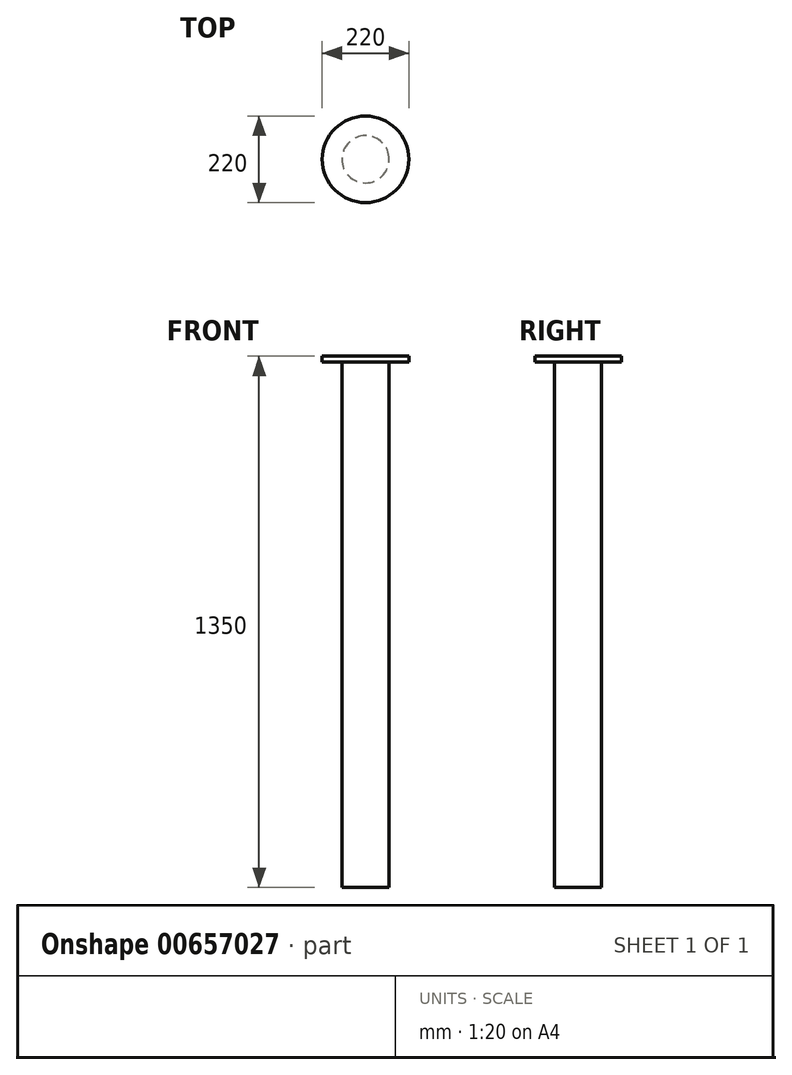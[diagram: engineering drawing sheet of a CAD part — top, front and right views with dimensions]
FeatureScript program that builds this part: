
annotation { "Feature Type Name" : "Feature", "Feature Type Description" : "" }
export const myFeature = defineFeature(function(context is Context, id is Id, definition is map)
    precondition{}
    {
        {
            var Q0;
            Q0=qCreatedBy(makeId("Top.planeOp"),FACE);
            var sketch = newSketch(context, id + "F0", { "sketchPlane" : qUnion([Q0])});
            skCircle(sketch, "E0", {"center": v(0, 0) * mm, "radius": 110 * mm});
            skCircle(sketch, "E1", {"center": v(0, 0) * mm, "radius": 60 * mm});
            skSolve(sketch);
        }
        {
            var Q0;
            Q0=qCreatedBy(makeId("Front.planeOp"),FACE);
            var sketch = newSketch(context, id + "F1", { "sketchPlane" : qUnion([Q0])});
            skLineSegment(sketch, "E2", {"start": v(0, 0) * mm, "end": v(0, -1350) * mm});
            skSolve(sketch);
        }
        {
            var Q0;
            Q0=makeQuery(id+"F0.imprint","IMPRINT",FACE,{"disambiguationData":[TD([[makeQuery(id+"F0.imprint","IMPRINT",EDGE,{"derivedFrom":sQuery(id+"F0.wireOp",EDGE,"E1")}),1.0]])]});
            var Q1;
            Q1=sQuery(id+"F1.wireOp",EDGE,"E2");
            sweep(context, id + "F2", {"profiles" : qUnion([Q0]), "path" : qUnion([Q1])});
        }
        {
            var Q0;
            Q0 = qSketchRegion(id + "F0", true);
            extrude(context, id + "F3", {"entities" : qUnion([Q0]), "operationType" : NewBodyOperationType.ADD, "oppositeDirection" : true, "depth" : 15 * mm, "offsetDistance" : 25 * mm});
        }
    });
